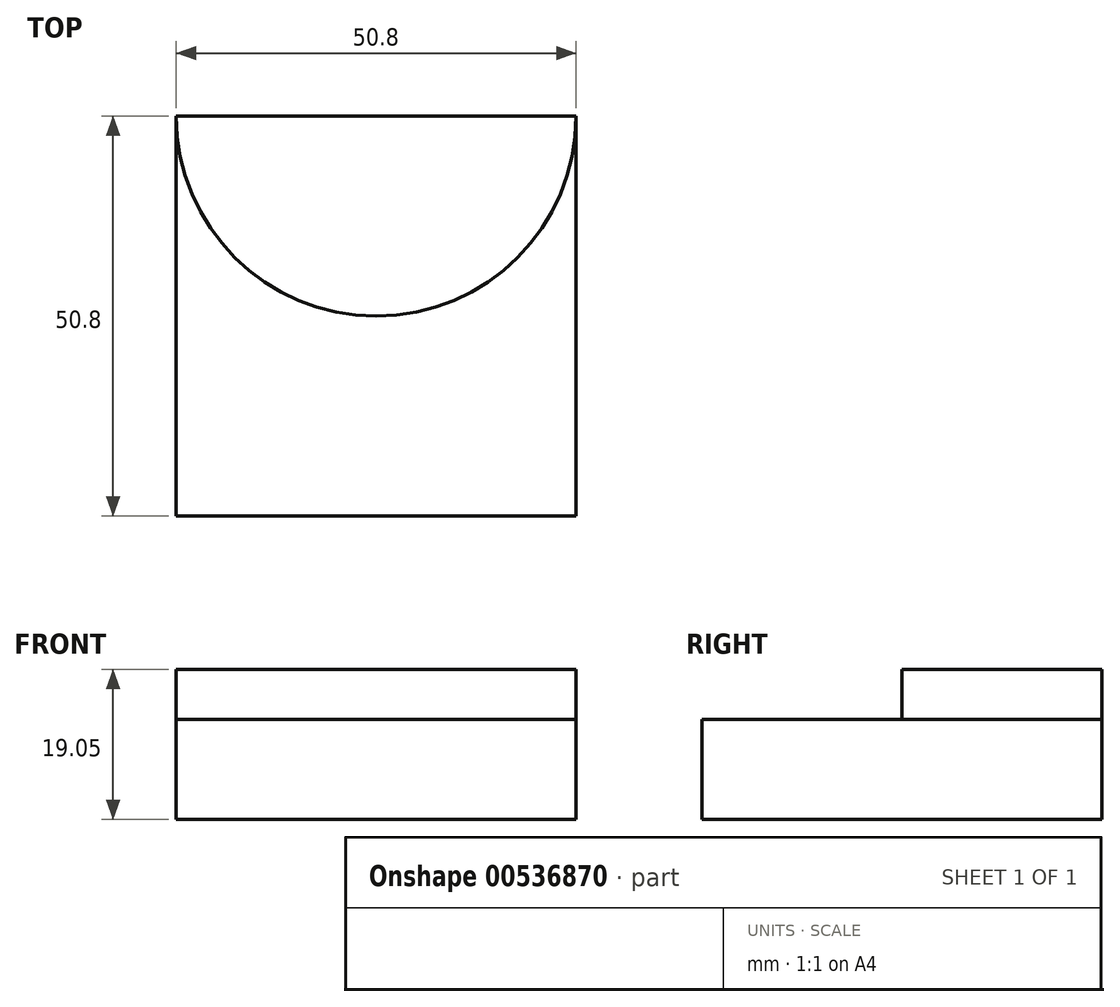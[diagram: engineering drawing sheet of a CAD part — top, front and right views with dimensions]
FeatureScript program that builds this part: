
annotation { "Feature Type Name" : "Feature", "Feature Type Description" : "" }
export const myFeature = defineFeature(function(context is Context, id is Id, definition is map)
    precondition{}
    {
        {
            var Q0;
            Q0=qCreatedBy(makeId("Top.planeOp"),FACE);
            var sketch = newSketch(context, id + "F0", { "sketchPlane" : qUnion([Q0])});
            skLineSegment(sketch, "E0.bottom", {"start": v(0, 0) * mm, "end": v(-50.8, 0) * mm});
            skLineSegment(sketch, "E0.top", {"start": v(0, 50.8) * mm, "end": v(-50.8, 50.8) * mm});
            skLineSegment(sketch, "E0.left", {"start": v(0, 0) * mm, "end": v(0, 50.8) * mm});
            skLineSegment(sketch, "E0.right", {"start": v(-50.8, 0) * mm, "end": v(-50.8, 50.8) * mm});
            skSolve(sketch);
        }
        {
            var Q0;
            Q0=makeQuery(id+"F0.imprint","IMPRINT",FACE,{"disambiguationData":[TD([[makeQuery(id+"F0.imprint","IMPRINT",EDGE,{"derivedFrom":sQuery(id+"F0.wireOp",EDGE,"E0.bottom")}),-1.0]])]});
            extrude(context, id + "F1", {"entities" : qUnion([Q0]), "oppositeDirection" : true, "depth" : 12.7 * mm, "offsetDistance" : 25.4 * mm});
        }
        {
            var Q0;
            Q0=makeQuery(id+"F1.opExtrude","CAP_FACE",FACE,{"disambiguationData":[OSD([sQuery(id+"F0.wireOp",EDGE,"E0.bottom"),sQuery(id+"F0.wireOp",EDGE,"E0.top"),sQuery(id+"F0.wireOp",EDGE,"E0.left"),sQuery(id+"F0.wireOp",EDGE,"E0.right")])],"isStart":true});
            var sketch = newSketch(context, id + "F2", { "sketchPlane" : qUnion([Q0])});
            skArc(sketch, "E1", {"start": v(-50.8, 50.8) * mm, "mid": v(-25.4, 25.4) * mm, "end": v(0, 50.8) * mm});
            skSolve(sketch);
        }
        {
            var Q0;
            Q0=makeQuery(id+"F2.imprint","IMPRINT",FACE,{"disambiguationData":[TD([[makeQuery(id+"F2.imprint","IMPRINT",EDGE,{"derivedFrom":sQuery(id+"F2.wireOp",EDGE,"E1")}),1.0]])]});
            extrude(context, id + "F3", {"entities" : qUnion([Q0]), "operationType" : NewBodyOperationType.ADD, "depth" : 6.35 * mm, "offsetDistance" : 25.4 * mm});
        }
    });
